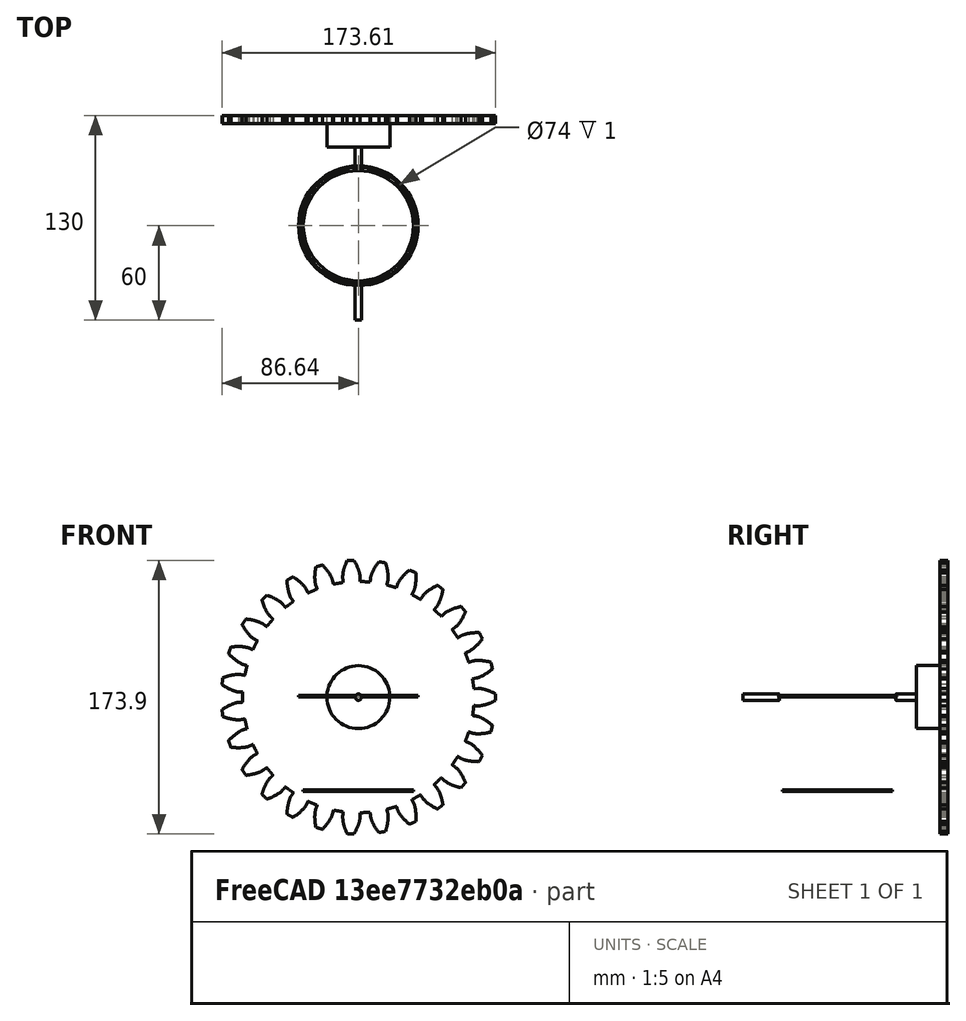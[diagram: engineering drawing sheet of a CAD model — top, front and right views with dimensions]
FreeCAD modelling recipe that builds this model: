
FCSTD DOCUMENT  (FreeCAD 0.20R29177 +233 (Git))
Label: proyecto-1
License: Creative Commons Attribution-ShareAlike
LicenseURL: http://creativecommons.org/licenses/by-sa/4.0/
objects: Part::Cylinder×6, Part::Cut×2, Part::RuledSurface×1, Part::MultiFuse×1, Part::FeaturePython×1
note: 11 computed .brp shape members not serialized (recipe doc carries the construction recipe); baked Part::Feature solids carry a one-line shape summary decoded from their .brp

FEATURE [Part::Cylinder] Cylinder  label="base"
  Angle = 360
  AttacherType = Attacher::AttachEngine3D
  FirstAngle = 0
  Height = 1
  Radius = 35
  SecondAngle = 0
FEATURE [Part::Cylinder] Cylinder001
  Angle = 360
  AttacherType = Attacher::AttachEngine3D
  FirstAngle = 0
  Height = 1
  Placement = pos=(0,0,60) rot=(0,0,1;0rad)
  Radius = 38
  SecondAngle = 0
FEATURE [Part::Cylinder] Cylinder002
  Angle = 360
  AttacherType = Attacher::AttachEngine3D
  FirstAngle = 0
  Height = 10
  Placement = pos=(0,0,60) rot=(0,0,1;0rad)
  Radius = 37
  SecondAngle = 0
FEATURE [Part::Cut] Cut  label="anillo superior"
  Base = -> Cylinder001
  Refine = true
  Tool = -> Cylinder002
FEATURE [Part::Cylinder] Cylinder003
  Angle = 360
  AttacherType = Attacher::AttachEngine3D
  FirstAngle = 0
  Height = 120
  Placement = pos=(0,60,60) rot=(1,0,0;1.5708rad)
  Radius = 2
  SecondAngle = 0
FEATURE [Part::Cylinder] Cylinder004
  Angle = 360
  AttacherType = Attacher::AttachEngine3D
  FirstAngle = 0
  Height = 30
  Placement = pos=(0,0,56) rot=(0,0,1;0rad)
  Radius = 37
  SecondAngle = 0
FEATURE [Part::Cut] Cut001
  Base = -> Cylinder003
  Refine = true
  Tool = -> Cylinder004
FEATURE [Part::RuledSurface] Ruled_Surface
  Curve1 = -> Cylinder [Edge3]
  Curve2 = -> Cut [Edge2]
  Orientation = 0
FEATURE [Part::Cylinder] Cylinder005
  Angle = 360
  AttacherType = Attacher::AttachEngine3D
  FirstAngle = 0
  Height = 20
  Placement = pos=(0,70,60) rot=(1,0,0;1.5708rad)
  Radius = 20
  SecondAngle = 0
FEATURE [Part::MultiFuse] Fusion  label="eje"
  Refine = true
  Shapes = -> [Cylinder005,Cut001]
FEATURE [Part::FeaturePython] InvoluteGear  label="engranaje-opcion"  # WARN: FeaturePython — macro-defined, semantics opaque (R4)
  AttacherType = Attacher::AttachEngine3D
  Placement = pos=(0,70,60) rot=(1,0,0;1.5708rad)
  angular_backlash = 0
  backlash = 0
  beta = 0
  clearance = 0.25
  da = 174
  df = 147
  double_helix = false
  dw = 162
  head = 0
  head_fillet = 0
  height = 5
  module = 6
  numpoints = 6
  pressure_angle = 20
  properties_from_tool = false
  reversed_backlash = false
  root_fillet = 0
  shift = 0
  simple = false
  teeth = 27
  transverse_pitch = 18.8496
  undercut = false
  version = 0.0.4
  expr: angular_backlash = backlash / dw * 360° / pi
  expr: dw = teeth * module
